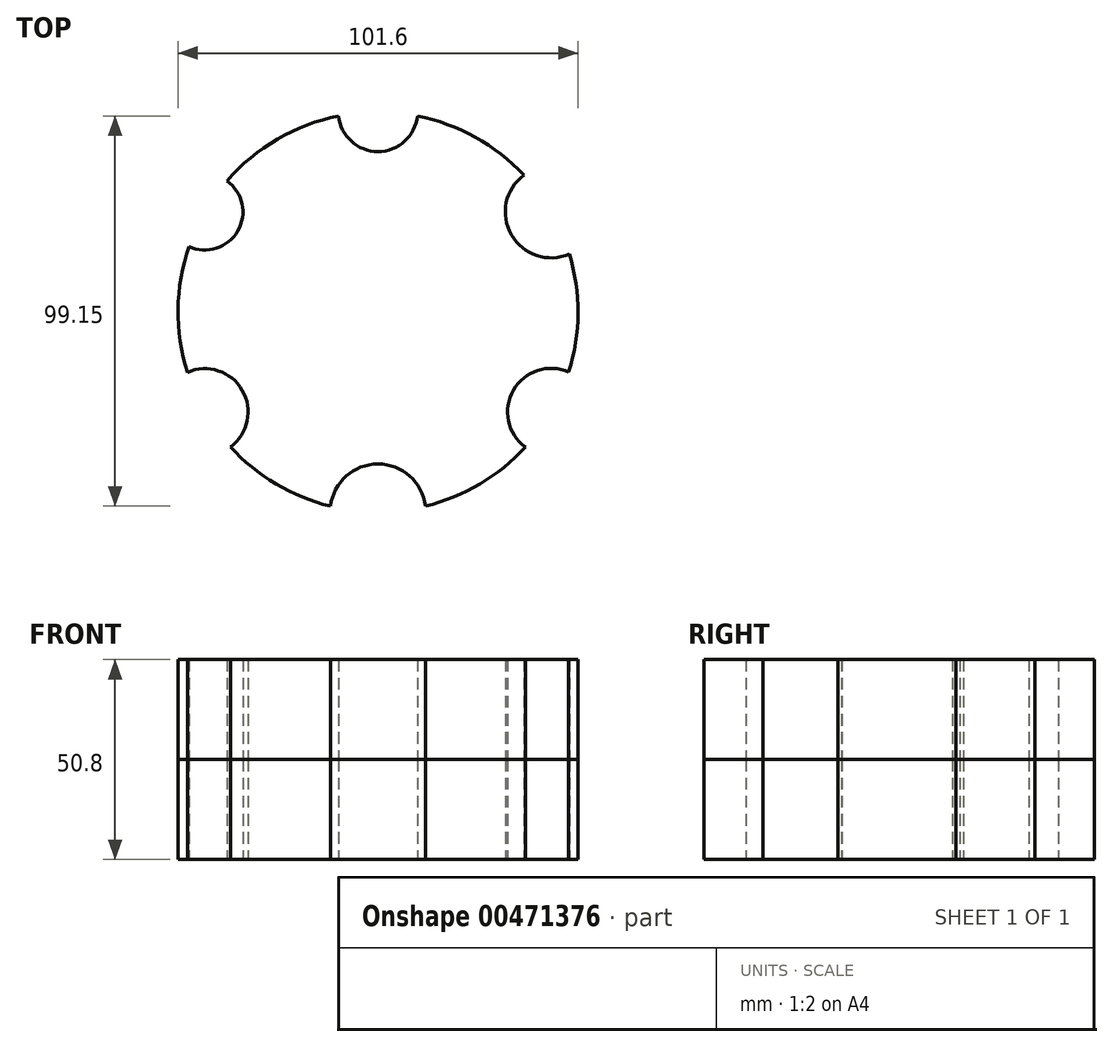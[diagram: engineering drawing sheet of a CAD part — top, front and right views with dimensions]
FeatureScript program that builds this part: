
annotation { "Feature Type Name" : "Feature", "Feature Type Description" : "" }
export const myFeature = defineFeature(function(context is Context, id is Id, definition is map)
    precondition{}
    {
        {
            var Q0;
            Q0=qCreatedBy(makeId("Top.planeOp"),FACE);
            var sketch = newSketch(context, id + "F0", { "sketchPlane" : qUnion([Q0])});
            skCircle(sketch, "E0", {"center": v(0, 0) * mm, "radius": 50.8 * mm});
            skCircle(sketch, "E1.cCircle", {"center": v(0, 0) * mm, "radius": 44 * mm, "construction": true});
            skLineSegment(sketch, "E1.0", {"start": v(-44, -25.4) * mm, "end": v(-44, 25.4) * mm, "construction": true});
            skLineSegment(sketch, "E1.1", {"start": v(-44, 25.4) * mm, "end": v(0, 50.8) * mm, "construction": true});
            skLineSegment(sketch, "E1.2", {"start": v(0, 50.8) * mm, "end": v(44, 25.4) * mm, "construction": true});
            skLineSegment(sketch, "E1.3", {"start": v(44, 25.4) * mm, "end": v(44, -25.4) * mm, "construction": true});
            skLineSegment(sketch, "E1.4", {"start": v(44, -25.4) * mm, "end": v(0, -50.8) * mm, "construction": true});
            skLineSegment(sketch, "E1.5", {"start": v(0, -50.8) * mm, "end": v(-44, -25.4) * mm, "construction": true});
            skPoint(sketch, "E1.0.midPoint", {"position": v(-44, 0) * mm});
            skCircle(sketch, "E2", {"center": v(-44, 25.4) * mm, "radius": 9.67 * mm});
            skCircle(sketch, "E3", {"center": v(-44, -25.4) * mm, "radius": 11 * mm});
            skCircle(sketch, "E4", {"center": v(0, -50.8) * mm, "radius": 12.16 * mm});
            skCircle(sketch, "E5", {"center": v(44, -25.4) * mm, "radius": 11.1 * mm});
            skCircle(sketch, "E6", {"center": v(44, 25.4) * mm, "radius": 11.65 * mm});
            skCircle(sketch, "E7", {"center": v(0, 50.8) * mm, "radius": 10.05 * mm});
            skSolve(sketch);
        }
        {
            var Q0;
            {var subQ1=sQuery(id+"F0.wireOp",EDGE,"E0");var subQ7=sQuery(id+"F0.wireOp",EDGE,"E6");var subQ14=makeQuery(id+"F0.imprint","INTERSECT",VERTEX,{"disambiguationData":[OD(0.0)],"derivedFrom":[subQ1,subQ7]});Q0=makeQuery(id+"F0.imprint","IMPRINT",FACE,{"disambiguationData":[TD([[makeQuery(id+"F0.imprint","IMPRINT",EDGE,{"disambiguationData":[TD([[subQ14,-1.0]])],"derivedFrom":subQ1}),1.0]])]});}
            extrude(context, id + "F1", {"entities" : qUnion([Q0]), "depth" : 25.4 * mm});
        }
        {
            var Q0;
            Q0=makeQuery(id+"F1.opExtrude","CAP_FACE",FACE,{"disambiguationData":[OSD([sQuery(id+"F0.wireOp",EDGE,"E0"),sQuery(id+"F0.wireOp",EDGE,"E2"),sQuery(id+"F0.wireOp",EDGE,"E3"),sQuery(id+"F0.wireOp",EDGE,"E4"),sQuery(id+"F0.wireOp",EDGE,"E5"),sQuery(id+"F0.wireOp",EDGE,"E6"),sQuery(id+"F0.wireOp",EDGE,"E7")])],"isStart":false});
            var sketch = newSketch(context, id + "F2", { "sketchPlane" : qUnion([Q0])});
            skArc(sketch, "E8.0.0", {"start": v(10, 49.8) * mm, "mid": v(0, 40.75) * mm, "end": v(-10, 49.8) * mm});
            skArc(sketch, "E8.0.1", {"start": v(-10, 49.8) * mm, "mid": v(-25.56, 43.9) * mm, "end": v(-38.38, 33.28) * mm});
            skArc(sketch, "E8.0.2", {"start": v(-38.38, 33.28) * mm, "mid": v(-35.62, 20.56) * mm, "end": v(-48.01, 16.6) * mm});
            skArc(sketch, "E8.0.3", {"start": v(-48.01, 16.6) * mm, "mid": v(-50.8, 0.67) * mm, "end": v(-48.43, -15.34) * mm});
            skArc(sketch, "E8.0.4", {"start": v(-48.43, -15.34) * mm, "mid": v(-34.47, -19.9) * mm, "end": v(-37.5, -34.27) * mm});
            skArc(sketch, "E8.0.5", {"start": v(-37.5, -34.27) * mm, "mid": v(-25.9, -43.7) * mm, "end": v(-12.07, -49.34) * mm});
            skArc(sketch, "E8.0.6", {"start": v(-12.07, -49.34) * mm, "mid": v(0, -38.64) * mm, "end": v(12.07, -49.34) * mm});
            skArc(sketch, "E8.0.7", {"start": v(12.07, -49.34) * mm, "mid": v(25.86, -43.72) * mm, "end": v(37.43, -34.34) * mm});
            skArc(sketch, "E8.0.8", {"start": v(37.43, -34.34) * mm, "mid": v(34.39, -19.85) * mm, "end": v(48.46, -15.24) * mm});
            skArc(sketch, "E8.0.9", {"start": v(48.46, -15.24) * mm, "mid": v(50.8, -0.28) * mm, "end": v(48.62, 14.7) * mm});
            skArc(sketch, "E8.0.10", {"start": v(48.62, 14.7) * mm, "mid": v(33.9, 19.57) * mm, "end": v(37.05, 34.76) * mm});
            skArc(sketch, "E8.0.11", {"start": v(37.05, 34.76) * mm, "mid": v(24.7, 44.4) * mm, "end": v(10, 49.8) * mm});
            skSolve(sketch);
        }
        {
            var Q0;
            Q0=makeQuery(id+"F2.imprint","IMPRINT",FACE,{"disambiguationData":[TD([[makeQuery(id+"F2.imprint","IMPRINT",EDGE,{"derivedFrom":sQuery(id+"F2.wireOp",EDGE,"E8.0.0")}),-1.0]])]});
            extrude(context, id + "F3", {"entities" : qUnion([Q0]), "depth" : 25.4 * mm});
        }
    });
